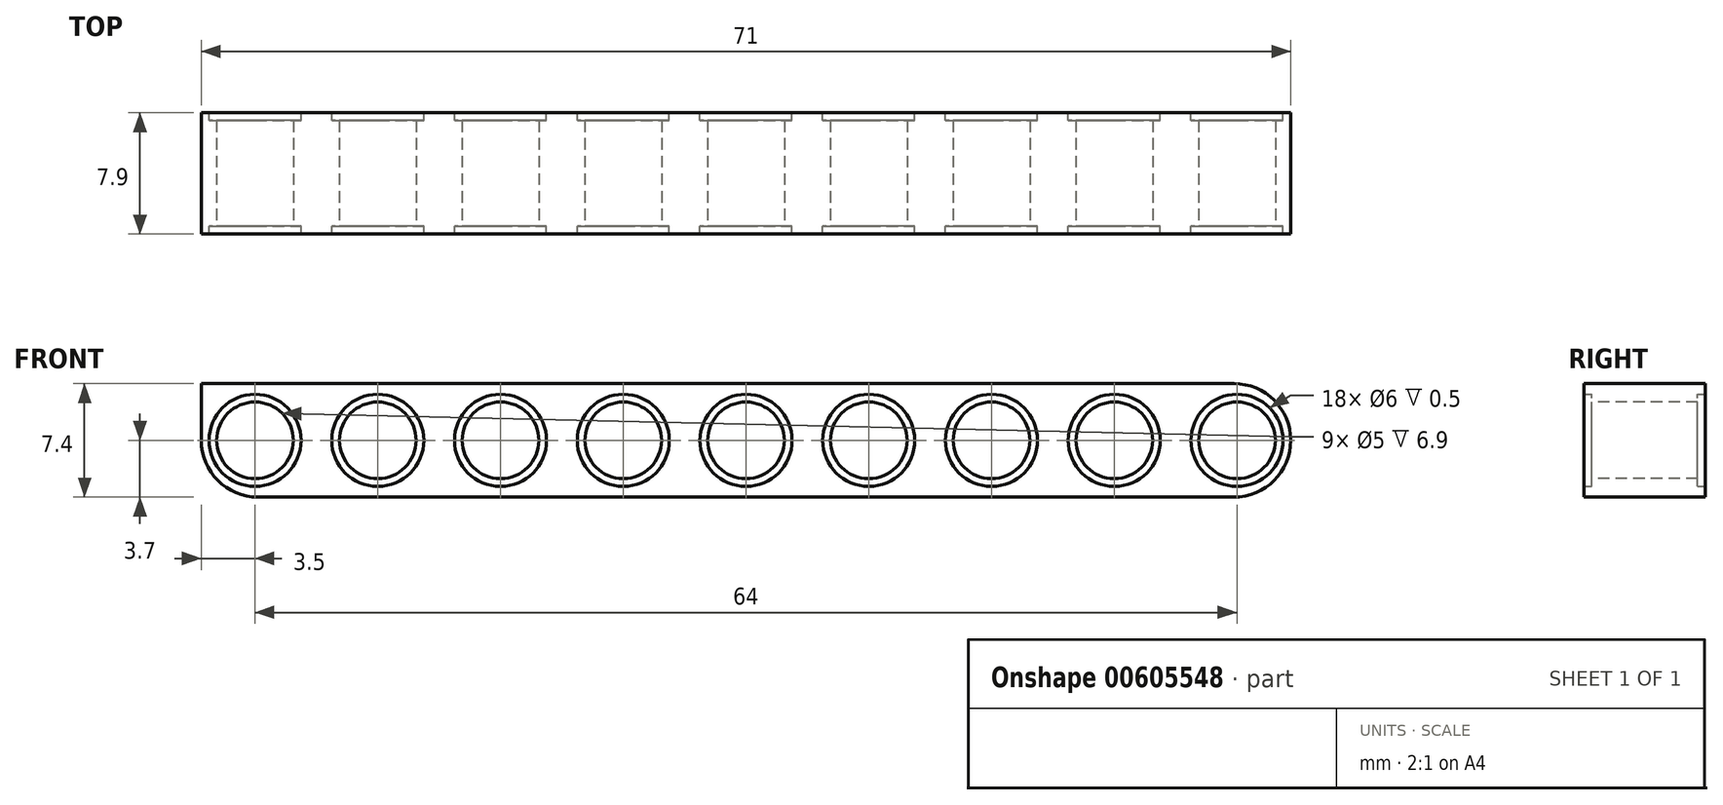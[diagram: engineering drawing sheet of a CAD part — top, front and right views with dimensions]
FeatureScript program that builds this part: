
annotation { "Feature Type Name" : "Feature", "Feature Type Description" : "" }
export const myFeature = defineFeature(function(context is Context, id is Id, definition is map)
    precondition{}
    {
        {
            var Q0;
            Q0=qCreatedBy(makeId("Front.planeOp"),FACE);
            var sketch = newSketch(context, id + "F0", { "sketchPlane" : qUnion([Q0])});
            skLineSegment(sketch, "E0", {"start": v(0, 0) * mm, "end": v(35.5, 0) * mm});
            skLineSegment(sketch, "E1", {"start": v(35.5, 0) * mm, "end": v(-35.5, 0) * mm});
            skLineSegment(sketch, "E2", {"start": v(-35.5, 0) * mm, "end": v(-35.5, 7.4) * mm});
            skLineSegment(sketch, "E3", {"start": v(-35.5, 7.4) * mm, "end": v(35.5, 7.4) * mm});
            skLineSegment(sketch, "E4", {"start": v(35.5, 7.4) * mm, "end": v(35.5, 0) * mm});
            skLineSegment(sketch, "E5", {"start": v(0, 0) * mm, "end": v(0, 3.7) * mm, "construction": true});
            skPoint(sketch, "E5.endSnap0", {"position": v(35.5, 3.7) * mm});
            skCircle(sketch, "E6", {"center": v(0, 3.7) * mm, "radius": 2.5 * mm});
            skCircle(sketch, "E7", {"center": v(0, 3.7) * mm, "radius": 3 * mm});
            skLineSegment(sketch, "E8.MirrorCS", {"start": v(35.5, 7.4) * mm, "end": v(-35.5, 7.4) * mm});
            skLineSegment(sketch, "E9.MirrorCS", {"start": v(-35.5, 7.4) * mm, "end": v(-35.5, 0) * mm});
            skLineSegment(sketch, "E10", {"start": v(0, 3.7) * mm, "end": v(8, 3.7) * mm, "construction": true});
            skLineSegment(sketch, "E11", {"start": v(8, 3.7) * mm, "end": v(16, 3.7) * mm, "construction": true});
            skLineSegment(sketch, "E12", {"start": v(16, 3.7) * mm, "end": v(24, 3.7) * mm, "construction": true});
            skLineSegment(sketch, "E13", {"start": v(24, 3.7) * mm, "end": v(32, 3.7) * mm, "construction": true});
            skLineSegment(sketch, "E14", {"start": v(0, 3.7) * mm, "end": v(-8, 3.7) * mm, "construction": true});
            skLineSegment(sketch, "E15", {"start": v(-8, 3.7) * mm, "end": v(-16, 3.7) * mm, "construction": true});
            skLineSegment(sketch, "E16", {"start": v(-16, 3.7) * mm, "end": v(-24, 3.7) * mm, "construction": true});
            skLineSegment(sketch, "E17", {"start": v(-24, 3.7) * mm, "end": v(-32, 3.7) * mm, "construction": true});
            skCircle(sketch, "E18", {"center": v(-32, 3.7) * mm, "radius": 3 * mm});
            skCircle(sketch, "E19", {"center": v(-24, 3.7) * mm, "radius": 3 * mm});
            skCircle(sketch, "E20", {"center": v(-16, 3.7) * mm, "radius": 3 * mm});
            skCircle(sketch, "E21", {"center": v(-8, 3.7) * mm, "radius": 3 * mm});
            skCircle(sketch, "E22", {"center": v(8, 3.7) * mm, "radius": 3 * mm});
            skCircle(sketch, "E23", {"center": v(16, 3.7) * mm, "radius": 3 * mm});
            skCircle(sketch, "E24", {"center": v(24, 3.7) * mm, "radius": 3 * mm});
            skCircle(sketch, "E25", {"center": v(32, 3.7) * mm, "radius": 3 * mm});
            skCircle(sketch, "E26", {"center": v(-32, 3.7) * mm, "radius": 2.5 * mm});
            skCircle(sketch, "E27", {"center": v(-24, 3.7) * mm, "radius": 2.5 * mm});
            skCircle(sketch, "E28", {"center": v(-16, 3.7) * mm, "radius": 2.5 * mm});
            skCircle(sketch, "E29", {"center": v(-8, 3.7) * mm, "radius": 2.5 * mm});
            skCircle(sketch, "E30", {"center": v(8, 3.7) * mm, "radius": 2.5 * mm});
            skCircle(sketch, "E31", {"center": v(16, 3.7) * mm, "radius": 2.5 * mm});
            skCircle(sketch, "E32", {"center": v(24, 3.7) * mm, "radius": 2.5 * mm});
            skCircle(sketch, "E33", {"center": v(32, 3.7) * mm, "radius": 2.5 * mm});
            skSolve(sketch);
        }
        {
            var Q0;
            {var subQ1=sQuery(id+"F0.wireOp",EDGE,"E4");Q0=makeQuery(id+"F0.imprint","IMPRINT",FACE,{"disambiguationData":[TD([[makeQuery(id+"F0.imprint","IMPRINT",EDGE,{"derivedFrom":subQ1}),-1.0]])]});}
            extrude(context, id + "F1", {"entities" : qUnion([Q0]), "endBound" : BoundingType.SYMMETRIC, "depth" : 7.9 * mm, "offsetDistance" : 25 * mm});
        }
        {
            var Q0;
            Q0=makeQuery(id+"F0.imprint","IMPRINT",FACE,{"disambiguationData":[TD([[makeQuery(id+"F0.imprint","IMPRINT",EDGE,{"derivedFrom":sQuery(id+"F0.wireOp",EDGE,"E18")}),1.0]])]});
            var Q1;
            Q1=makeQuery(id+"F0.imprint","IMPRINT",FACE,{"disambiguationData":[TD([[makeQuery(id+"F0.imprint","IMPRINT",EDGE,{"derivedFrom":sQuery(id+"F0.wireOp",EDGE,"E19")}),1.0]])]});
            var Q2;
            Q2=makeQuery(id+"F0.imprint","IMPRINT",FACE,{"disambiguationData":[TD([[makeQuery(id+"F0.imprint","IMPRINT",EDGE,{"derivedFrom":sQuery(id+"F0.wireOp",EDGE,"E20")}),1.0]])]});
            var Q3;
            Q3=makeQuery(id+"F0.imprint","IMPRINT",FACE,{"disambiguationData":[TD([[makeQuery(id+"F0.imprint","IMPRINT",EDGE,{"derivedFrom":sQuery(id+"F0.wireOp",EDGE,"E21")}),1.0]])]});
            var Q4;
            Q4=makeQuery(id+"F0.imprint","IMPRINT",FACE,{"disambiguationData":[TD([[makeQuery(id+"F0.imprint","IMPRINT",EDGE,{"derivedFrom":sQuery(id+"F0.wireOp",EDGE,"E6")}),-1.0]])]});
            var Q5;
            Q5=makeQuery(id+"F0.imprint","IMPRINT",FACE,{"disambiguationData":[TD([[makeQuery(id+"F0.imprint","IMPRINT",EDGE,{"derivedFrom":sQuery(id+"F0.wireOp",EDGE,"E22")}),1.0]])]});
            var Q6;
            Q6=makeQuery(id+"F0.imprint","IMPRINT",FACE,{"disambiguationData":[TD([[makeQuery(id+"F0.imprint","IMPRINT",EDGE,{"derivedFrom":sQuery(id+"F0.wireOp",EDGE,"E23")}),1.0]])]});
            var Q7;
            Q7=makeQuery(id+"F0.imprint","IMPRINT",FACE,{"disambiguationData":[TD([[makeQuery(id+"F0.imprint","IMPRINT",EDGE,{"derivedFrom":sQuery(id+"F0.wireOp",EDGE,"E24")}),1.0]])]});
            var Q8;
            Q8=makeQuery(id+"F0.imprint","IMPRINT",FACE,{"disambiguationData":[TD([[makeQuery(id+"F0.imprint","IMPRINT",EDGE,{"derivedFrom":sQuery(id+"F0.wireOp",EDGE,"E25")}),1.0]])]});
            extrude(context, id + "F2", {"entities" : qUnion([Q0, Q1, Q2, Q3, Q4, Q5, Q6, Q7, Q8]), "operationType" : NewBodyOperationType.ADD, "endBound" : BoundingType.SYMMETRIC, "oppositeDirection" : true, "depth" : 6.9 * mm, "offsetDistance" : 25 * mm});
        }
        {
            var Q0;
            Q0=makeQuery(id+"F1.opExtrude","SWEPT_EDGE",EDGE,{"disambiguationData":[OSD([sQuery(id+"F0.wireOp",EDGE,"E8.MirrorCS"),sQuery(id+"F0.wireOp",EDGE,"E9.MirrorCS")])]});
            var Q1;
            Q1=makeQuery(id+"F1.opExtrude","SWEPT_EDGE",EDGE,{"disambiguationData":[OSD([sQuery(id+"F0.wireOp",EDGE,"E1"),sQuery(id+"F0.wireOp",EDGE,"E9.MirrorCS")])]});
            fillet(context, id + "F3", {"entities" : qUnion([Q0, Q1]), "radius" : 3.7 * mm, "tangentPropagation" : true, "allowEdgeOverflow" : false});
        }
        {
            var Q0;
            Q0=makeQuery(id+"F1.opExtrude","SWEPT_EDGE",EDGE,{"disambiguationData":[OSD([sQuery(id+"F0.wireOp",EDGE,"E4"),sQuery(id+"F0.wireOp",EDGE,"E8.MirrorCS")])]});
            var Q1;
            Q1=makeQuery(id+"F1.opExtrude","SWEPT_EDGE",EDGE,{"disambiguationData":[OSD([sQuery(id+"F0.wireOp",EDGE,"E1"),sQuery(id+"F0.wireOp",EDGE,"E4")])]});
            fillet(context, id + "F4", {"entities" : qUnion([Q0, Q1]), "radius" : 3.7 * mm, "tangentPropagation" : true, "allowEdgeOverflow" : false});
        }
    });
